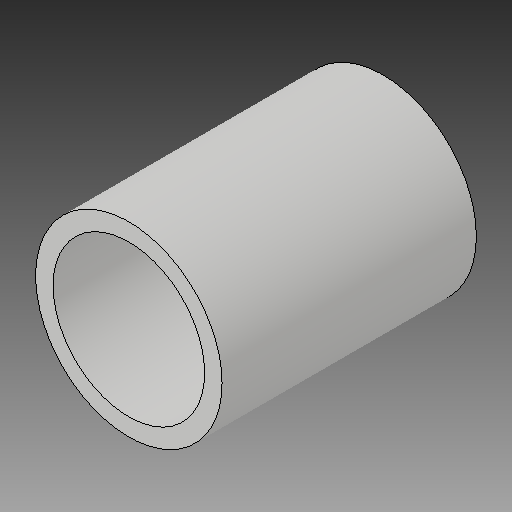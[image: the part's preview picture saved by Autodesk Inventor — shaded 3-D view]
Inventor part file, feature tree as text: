
AUTODESK INVENTOR PART (.ipt)
format: ipt  version: 2018 (Build 220112000, 112)  size: 108,544 bytes
history: native  units: mm
features: extrude x1, sketch x1
ambient origin geometry x8: Origin, YZ Plane, XZ Plane, XY Plane, X Axis, Y Axis, Z Axis, Center Point
bodies: Solid1 (feature_tree)
feature tree (2):
  extrude  "Extrusion1"  Depth=21.824mm
  sketch  "Sketch1"  dims[d0=16.0mm d1=13.0mm d2=21.824mm d3=0.0mm]
